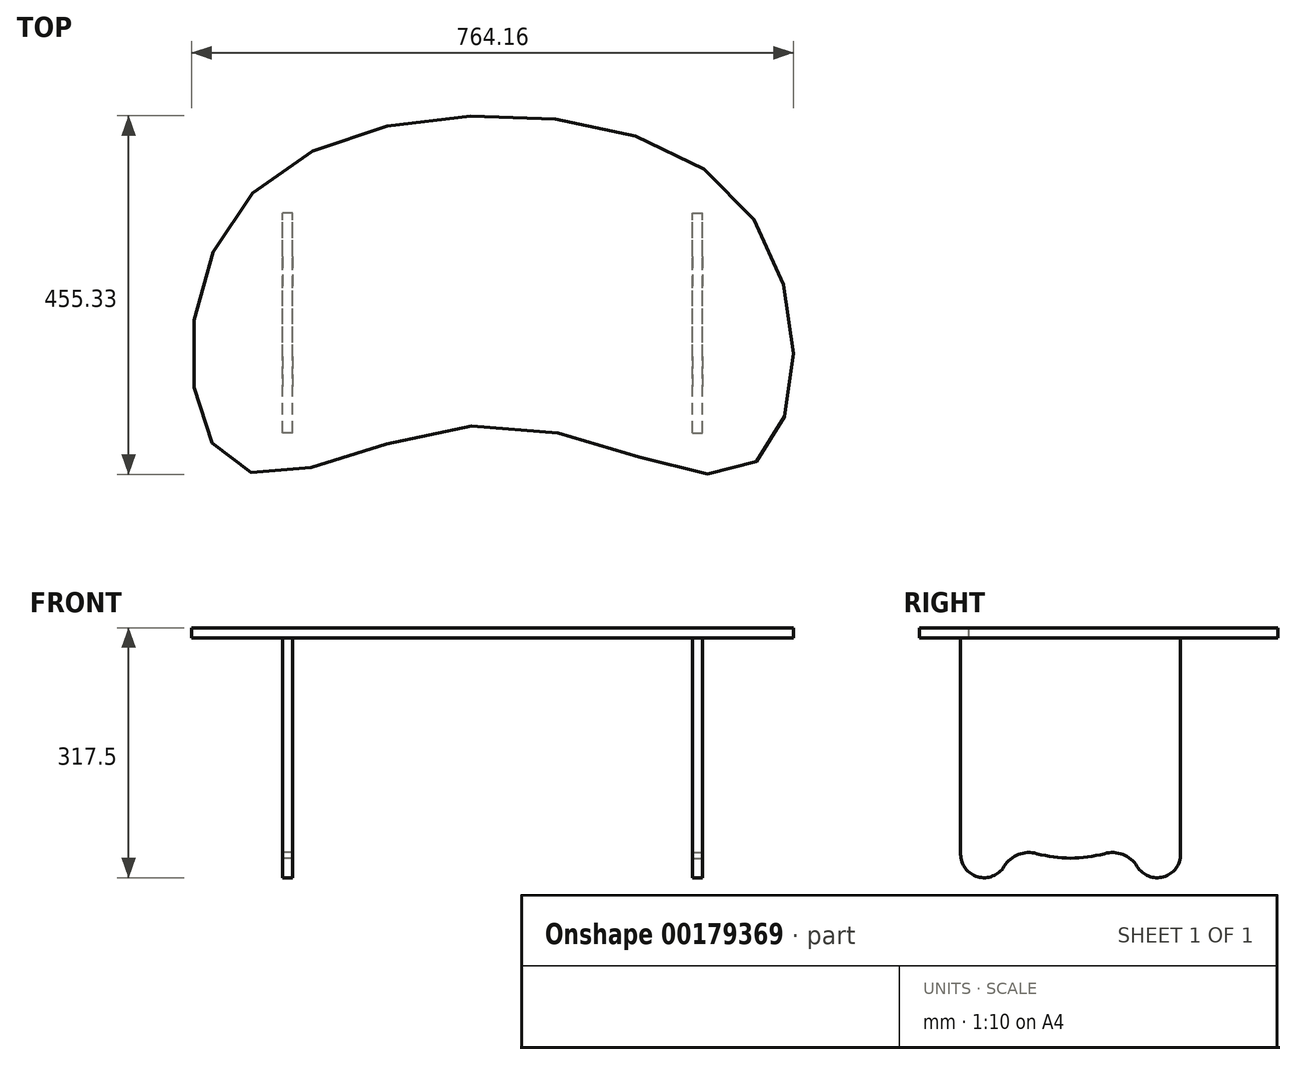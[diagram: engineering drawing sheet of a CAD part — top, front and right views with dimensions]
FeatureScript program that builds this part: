
annotation { "Feature Type Name" : "Feature", "Feature Type Description" : "" }
export const myFeature = defineFeature(function(context is Context, id is Id, definition is map)
    precondition{}
    {
        {
            var Q0;
            Q0=qCreatedBy(makeId("Top.planeOp"),FACE);
            var sketch = newSketch(context, id + "F0", { "sketchPlane" : qUnion([Q0])});
            skLineSegment(sketch, "E0.bottom", {"start": v(-304.8, 177.8) * mm, "end": v(304.8, 177.8) * mm, "construction": true});
            skLineSegment(sketch, "E0.top", {"start": v(-304.8, -177.8) * mm, "end": v(304.8, -177.8) * mm, "construction": true});
            skLineSegment(sketch, "E0.left", {"start": v(-304.8, 177.8) * mm, "end": v(-304.8, -177.8) * mm, "construction": true});
            skLineSegment(sketch, "E0.right", {"start": v(304.8, 177.8) * mm, "end": v(304.8, -177.8) * mm, "construction": true});
            skLineSegment(sketch, "E1", {"start": v(304.8, 177.8) * mm, "end": v(-304.8, -177.8) * mm, "construction": true});
            skPoint(sketch, "E2", {"position": v(0, 0) * mm});
            skFitSpline(sketch, "E3", {"points": [v(-304.8, 177.8) * mm, v(0, 275.73) * mm, v(304.8, 177.8) * mm, v(380.57, -58.24) * mm, v(304.8, -177.8) * mm, v(0, -116.95) * mm, v(-304.8, -177.8) * mm, v(-380.57, -58.24) * mm, v(-304.8, 177.8) * mm]});
            skLineSegment(sketch, "E4", {"start": v(-380.57, -58.24) * mm, "end": v(0, 0) * mm, "construction": true});
            skLineSegment(sketch, "E5", {"start": v(380.57, -58.24) * mm, "end": v(0, 0) * mm, "construction": true});
            skSolve(sketch);
        }
        {
            var Q0;
            Q0=makeQuery(id+"F0.imprint","IMPRINT",FACE,{"disambiguationData":[TD([[makeQuery(id+"F0.imprint","IMPRINT",EDGE,{"derivedFrom":sQuery(id+"F0.wireOp",EDGE,"E3")}),-1.0]])]});
            extrude(context, id + "F1", {"entities" : qUnion([Q0]), "depth" : 12.7 * mm});
        }
        {
            var Q0;
            Q0=makeQuery(id+"F1.opExtrude","CAP_FACE",FACE,{"disambiguationData":[OSD([sQuery(id+"F0.wireOp",EDGE,"E3")])],"isStart":true});
            var sketch = newSketch(context, id + "F2", { "sketchPlane" : qUnion([Q0])});
            skLineSegment(sketch, "E6.bottom", {"start": v(254, 127) * mm, "end": v(266.7, 127) * mm});
            skLineSegment(sketch, "E6.top", {"start": v(254, -152.4) * mm, "end": v(266.7, -152.4) * mm});
            skLineSegment(sketch, "E6.left", {"start": v(254, 127) * mm, "end": v(254, -152.4) * mm});
            skLineSegment(sketch, "E6.right", {"start": v(266.7, 127) * mm, "end": v(266.7, -152.4) * mm});
            skSolve(sketch);
        }
        {
            var Q0;
            Q0 = qSketchRegion(id + "F2", true);
            extrude(context, id + "F3", {"entities" : qUnion([Q0]), "operationType" : NewBodyOperationType.ADD, "depth" : 304.8 * mm});
        }
        {
            var Q0;
            Q0=makeQuery(id+"F3.opExtrude","SWEPT_FACE",FACE,{"disambiguationData":[OSD([sQuery(id+"F2.wireOp",EDGE,"E6.right")])]});
            var sketch = newSketch(context, id + "F4", { "sketchPlane" : qUnion([Q0])});
            skCircle(sketch, "E7", {"center": v(-97.17, -274.97) * mm, "radius": 29.83 * mm});
            skCircle(sketch, "E8", {"center": v(122.57, -274.97) * mm, "radius": 29.83 * mm});
            skCircle(sketch, "E9", {"center": v(12.7, -119.54) * mm, "radius": 160.51 * mm});
            skCircle(sketch, "E10", {"center": v(-40.02, -310.22) * mm, "radius": 37.32 * mm});
            skCircle(sketch, "E11", {"center": v(65.42, -310.22) * mm, "radius": 37.32 * mm});
            skSolve(sketch);
        }
        {
            var Q0;
            {var subQ0=sQuery(id+"F4.wireOp",EDGE,"E8");var subQ1=sQuery(id+"F2.wireOp",EDGE,"E6.right");var subQ4=makeQuery(id+"F3.opExtrude","CAP_EDGE",EDGE,{"disambiguationData":[OSD([subQ1])],"isStart":false});var subQ5=makeQuery(id+"F4.imprint","INTERSECT",VERTEX,{"derivedFrom":[subQ4,subQ0]});Q0=makeQuery(id+"F4.imprint","IMPRINT",FACE,{"disambiguationData":[TD([[makeQuery(id+"F4.imprint","IMPRINT",EDGE,{"disambiguationData":[TD([[subQ5,-1.0]])],"derivedFrom":subQ0}),-1.0]])]});}
            var Q1;
            {var subQ0=sQuery(id+"F4.wireOp",EDGE,"E11");var subQ1=sQuery(id+"F4.wireOp",EDGE,"E8");var subQ2=makeQuery(id+"F4.imprint","INTERSECT",VERTEX,{"derivedFrom":[subQ1,subQ0]});Q1=makeQuery(id+"F4.imprint","IMPRINT",FACE,{"disambiguationData":[TD([[makeQuery(id+"F4.imprint","IMPRINT",EDGE,{"disambiguationData":[TD([[subQ2,-1.0]])],"derivedFrom":subQ1}),-1.0]])]});}
            var Q2;
            {var subQ0=sQuery(id+"F4.wireOp",EDGE,"E11");var subQ1=makeQuery(id+"F4.imprint","INTERSECT",VERTEX,{"derivedFrom":[sQuery(id+"F4.wireOp",EDGE,"E8"),subQ0]});Q2=makeQuery(id+"F4.imprint","IMPRINT",FACE,{"disambiguationData":[TD([[makeQuery(id+"F4.imprint","IMPRINT",EDGE,{"disambiguationData":[TD([[subQ1,1.0]])],"derivedFrom":subQ0}),1.0]])]});}
            var Q3;
            {var subQ0=sQuery(id+"F4.wireOp",EDGE,"E10");var subQ1=sQuery(id+"F4.wireOp",EDGE,"E9");var subQ2=makeQuery(id+"F4.imprint","INTERSECT",VERTEX,{"derivedFrom":[subQ1,subQ0]});Q3=makeQuery(id+"F4.imprint","IMPRINT",FACE,{"disambiguationData":[TD([[makeQuery(id+"F4.imprint","IMPRINT",EDGE,{"disambiguationData":[TD([[subQ2,-1.0]])],"derivedFrom":subQ1}),-1.0]])]});}
            var Q4;
            {var subQ0=sQuery(id+"F4.wireOp",EDGE,"E10");var subQ1=makeQuery(id+"F4.imprint","INTERSECT",VERTEX,{"derivedFrom":[sQuery(id+"F4.wireOp",EDGE,"E9"),subQ0]});Q4=makeQuery(id+"F4.imprint","IMPRINT",FACE,{"disambiguationData":[TD([[makeQuery(id+"F4.imprint","IMPRINT",EDGE,{"disambiguationData":[TD([[subQ1,1.0]])],"derivedFrom":subQ0}),1.0]])]});}
            var Q5;
            {var subQ0=sQuery(id+"F4.wireOp",EDGE,"E10");var subQ1=sQuery(id+"F4.wireOp",EDGE,"E7");var subQ2=makeQuery(id+"F4.imprint","INTERSECT",VERTEX,{"derivedFrom":[subQ1,subQ0]});Q5=makeQuery(id+"F4.imprint","IMPRINT",FACE,{"disambiguationData":[TD([[makeQuery(id+"F4.imprint","IMPRINT",EDGE,{"disambiguationData":[TD([[subQ2,1.0]])],"derivedFrom":subQ1}),-1.0]])]});}
            var Q6;
            {var subQ0=sQuery(id+"F4.wireOp",EDGE,"E7");var subQ1=sQuery(id+"F2.wireOp",EDGE,"E6.right");var subQ4=makeQuery(id+"F3.opExtrude","CAP_EDGE",EDGE,{"disambiguationData":[OSD([subQ1])],"isStart":false});var subQ5=makeQuery(id+"F4.imprint","INTERSECT",VERTEX,{"derivedFrom":[subQ4,subQ0]});Q6=makeQuery(id+"F4.imprint","IMPRINT",FACE,{"disambiguationData":[TD([[makeQuery(id+"F4.imprint","IMPRINT",EDGE,{"disambiguationData":[TD([[subQ5,1.0]])],"derivedFrom":subQ0}),-1.0]])]});}
            extrude(context, id + "F5", {"entities" : qUnion([Q0, Q1, Q2, Q3, Q4, Q5, Q6]), "operationType" : NewBodyOperationType.REMOVE, "endBound" : BoundingType.THROUGH_ALL, "oppositeDirection" : true, "depth" : 12.7 * mm});
        }
        {
            var Q0;
            Q0=makeQuery(id+"F1.opExtrude","SWEPT_BODY",BODY,{"disambiguationData":[OSD([sQuery(id+"F0.wireOp",EDGE,"E3")])]});
            var Q1;
            Q1=qCreatedBy(makeId("Right.planeOp"),FACE);
            mirror(context, id + "F6", {"operationType" : NewBodyOperationType.ADD, "entities" : qUnion([Q0]), "mirrorPlane" : qUnion([Q1])});
        }
    });
